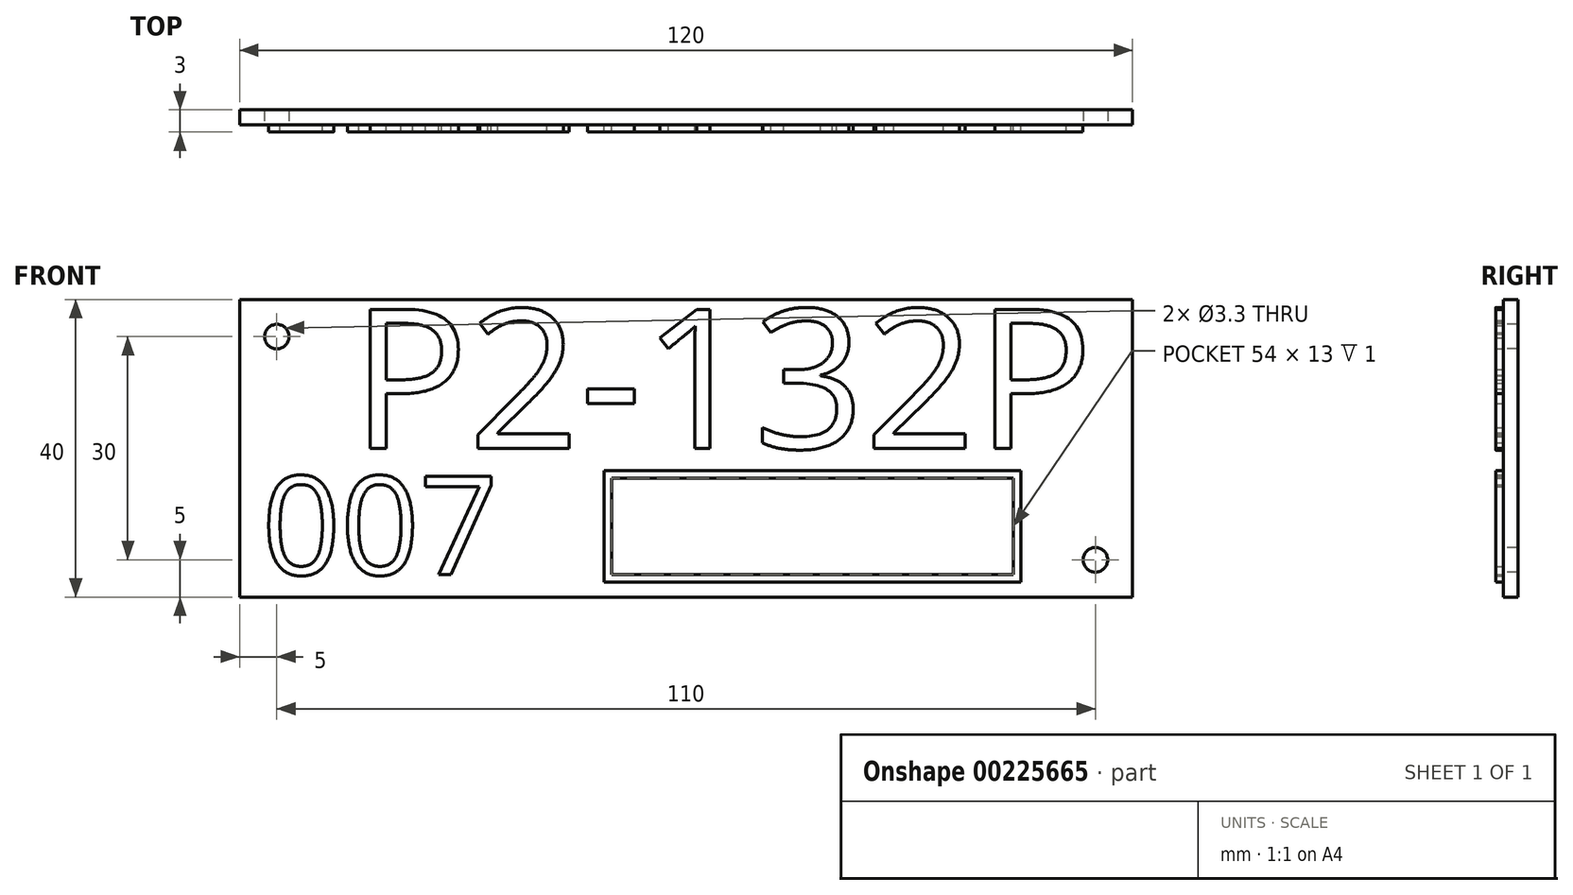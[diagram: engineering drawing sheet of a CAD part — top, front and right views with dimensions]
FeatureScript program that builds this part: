
annotation { "Feature Type Name" : "Feature", "Feature Type Description" : "" }
export const myFeature = defineFeature(function(context is Context, id is Id, definition is map)
    precondition{}
    {
        {
            var Q0;
            Q0=qCreatedBy(makeId("Front.planeOp"),FACE);
            var sketch = newSketch(context, id + "F0", { "sketchPlane" : qUnion([Q0])});
            skLineSegment(sketch, "E0.bottom", {"start": v(60, -20) * mm, "end": v(-60, -20) * mm});
            skLineSegment(sketch, "E0.top", {"start": v(60, 20) * mm, "end": v(-60, 20) * mm});
            skLineSegment(sketch, "E0.left", {"start": v(60, -20) * mm, "end": v(60, 20) * mm});
            skLineSegment(sketch, "E0.right", {"start": v(-60, -20) * mm, "end": v(-60, 20) * mm});
            skPoint(sketch, "E0.middle", {"position": v(0, 0) * mm});
            skSolve(sketch);
        }
        {
            var Q0;
            Q0=makeQuery(id+"F0.imprint","IMPRINT",FACE,{"disambiguationData":[TD([[makeQuery(id+"F0.imprint","IMPRINT",EDGE,{"derivedFrom":sQuery(id+"F0.wireOp",EDGE,"E0.bottom")}),-1.0]])]});
            extrude(context, id + "F1", {"entities" : qUnion([Q0]), "depth" : 2 * mm});
        }
        {
            var Q0;
            Q0=makeQuery(id+"F1.opExtrude","CAP_FACE",FACE,{"disambiguationData":[OSD([sQuery(id+"F0.wireOp",EDGE,"E0.bottom"),sQuery(id+"F0.wireOp",EDGE,"E0.top"),sQuery(id+"F0.wireOp",EDGE,"E0.left"),sQuery(id+"F0.wireOp",EDGE,"E0.right")])],"isStart":false});
            var sketch = newSketch(context, id + "F2", { "sketchPlane" : qUnion([Q0])});
            skPoint(sketch, "E1", {"position": v(-55, 15) * mm});
            skPoint(sketch, "E2", {"position": v(55, -15) * mm});
            skSolve(sketch);
        }
        {
            var Q0;
            Q0=sQuery(id+"F2.wireOp",VERTEX,"E1");
            var Q1;
            Q1=sQuery(id+"F2.wireOp",VERTEX,"E2");
            var Q2;
            Q2=makeQuery(id+"F1.opExtrude","SWEPT_BODY",BODY,{"disambiguationData":[OSD([sQuery(id+"F0.wireOp",EDGE,"E0.bottom"),sQuery(id+"F0.wireOp",EDGE,"E0.top"),sQuery(id+"F0.wireOp",EDGE,"E0.left"),sQuery(id+"F0.wireOp",EDGE,"E0.right")])]});
            hole(context, id + "F3", {"style" : HoleStyle.SIMPLE, "endStyle" : HoleEndStyle.THROUGH, "holeDiameter" : 3.3 * mm, "locations" : qUnion([Q0, Q1]), "scope" : qUnion([Q2]), "isTappedThrough" : true});
        }
        {
            var Q0;
            Q0=makeQuery(id+"F1.opExtrude","CAP_FACE",FACE,{"disambiguationData":[OSD([sQuery(id+"F0.wireOp",EDGE,"E0.bottom"),sQuery(id+"F0.wireOp",EDGE,"E0.top"),sQuery(id+"F0.wireOp",EDGE,"E0.left"),sQuery(id+"F0.wireOp",EDGE,"E0.right")])],"isStart":false});
            var sketch = newSketch(context, id + "F4", { "sketchPlane" : qUnion([Q0])});
            skText(sketch, "E3", { "text": "P2-132P", "fontName": "OpenSans-Regular.ttf"});
            const initialGuessF4  = {"E3": [-0.045, 0, 1, 0, 0.01882]};
            skSetInitialGuess(sketch, initialGuessF4);
            skSolve(sketch);
        }
        {
            var Q0;
            Q0 = qSketchRegion(id + "F4", true);
            extrude(context, id + "F5", {"entities" : qUnion([Q0]), "operationType" : NewBodyOperationType.ADD, "depth" : 1 * mm});
        }
        {
            var Q0;
            {var subQ0=sQuery(id+"F0.wireOp",EDGE,"E0.top");var subQ1=sQuery(id+"F0.wireOp",EDGE,"E0.left");var subQ2=sQuery(id+"F0.wireOp",EDGE,"E0.right");var subQ3=sQuery(id+"F0.wireOp",EDGE,"E0.bottom");Q0=makeQuery(id+"F5.boolean.opBoolean","SPLIT",FACE,{"disambiguationData":[TD([makeQuery(id+"F1.opExtrude","SWEPT_FACE",FACE,{"disambiguationData":[OSD([subQ3])]})])],"derivedFrom":makeQuery(id+"F1.opExtrude","CAP_FACE",FACE,{"disambiguationData":[OSD([subQ3,subQ0,subQ1,subQ2])],"isStart":false})});}
            var sketch = newSketch(context, id + "F6", { "sketchPlane" : qUnion([Q0])});
            skText(sketch, "E4", { "text": "007", "fontName": "OpenSans-Regular.ttf"});
            const initialGuessF6  = {"E4": [-0.057, -0.017, 1, 0, 0.01332]};
            skSetInitialGuess(sketch, initialGuessF6);
            skSolve(sketch);
        }
        {
            var Q0;
            Q0 = qSketchRegion(id + "F6", true);
            extrude(context, id + "F7", {"entities" : qUnion([Q0]), "operationType" : NewBodyOperationType.ADD, "depth" : 1 * mm});
        }
        {
            var Q0;
            {var subQ46=sQuery(id+"F0.wireOp",EDGE,"E0.top");var subQ48=sQuery(id+"F0.wireOp",EDGE,"E0.left");var subQ66=sQuery(id+"F0.wireOp",EDGE,"E0.right");var subQ76=sQuery(id+"F0.wireOp",EDGE,"E0.bottom");var subQ77=makeQuery(id+"F1.opExtrude","SWEPT_FACE",FACE,{"disambiguationData":[OSD([subQ76])]});Q0=makeQuery(id+"F7.boolean.opBoolean","SPLIT",FACE,{"disambiguationData":[TD([subQ77])],"derivedFrom":makeQuery(id+"F5.boolean.opBoolean","SPLIT",FACE,{"disambiguationData":[TD([subQ77])],"derivedFrom":makeQuery(id+"F1.opExtrude","CAP_FACE",FACE,{"disambiguationData":[OSD([subQ76,subQ46,subQ48,subQ66])],"isStart":false})})});}
            var sketch = newSketch(context, id + "F8", { "sketchPlane" : qUnion([Q0])});
            skLineSegment(sketch, "E5.bottom", {"start": v(45, -18) * mm, "end": v(-11, -18) * mm});
            skLineSegment(sketch, "E5.top", {"start": v(45, -3) * mm, "end": v(-11, -3) * mm});
            skLineSegment(sketch, "E5.left", {"start": v(45, -18) * mm, "end": v(45, -3) * mm});
            skLineSegment(sketch, "E5.right", {"start": v(-11, -18) * mm, "end": v(-11, -3) * mm});
            skPoint(sketch, "E5.middle", {"position": v(17, -10.5) * mm});
            skLineSegment(sketch, "E6.0", {"start": v(44, -4) * mm, "end": v(-10, -4) * mm});
            skLineSegment(sketch, "E6.1", {"start": v(44, -17) * mm, "end": v(44, -4) * mm});
            skLineSegment(sketch, "E6.2", {"start": v(44, -17) * mm, "end": v(-10, -17) * mm});
            skLineSegment(sketch, "E6.3", {"start": v(-10, -17) * mm, "end": v(-10, -4) * mm});
            skSolve(sketch);
        }
        {
            var Q0;
            Q0=makeQuery(id+"F8.imprint","IMPRINT",FACE,{"disambiguationData":[TD([[makeQuery(id+"F8.imprint","IMPRINT",EDGE,{"derivedFrom":sQuery(id+"F8.wireOp",EDGE,"E5.bottom")}),-1.0]])]});
            extrude(context, id + "F9", {"entities" : qUnion([Q0]), "operationType" : NewBodyOperationType.ADD, "depth" : 1 * mm});
        }
    });
